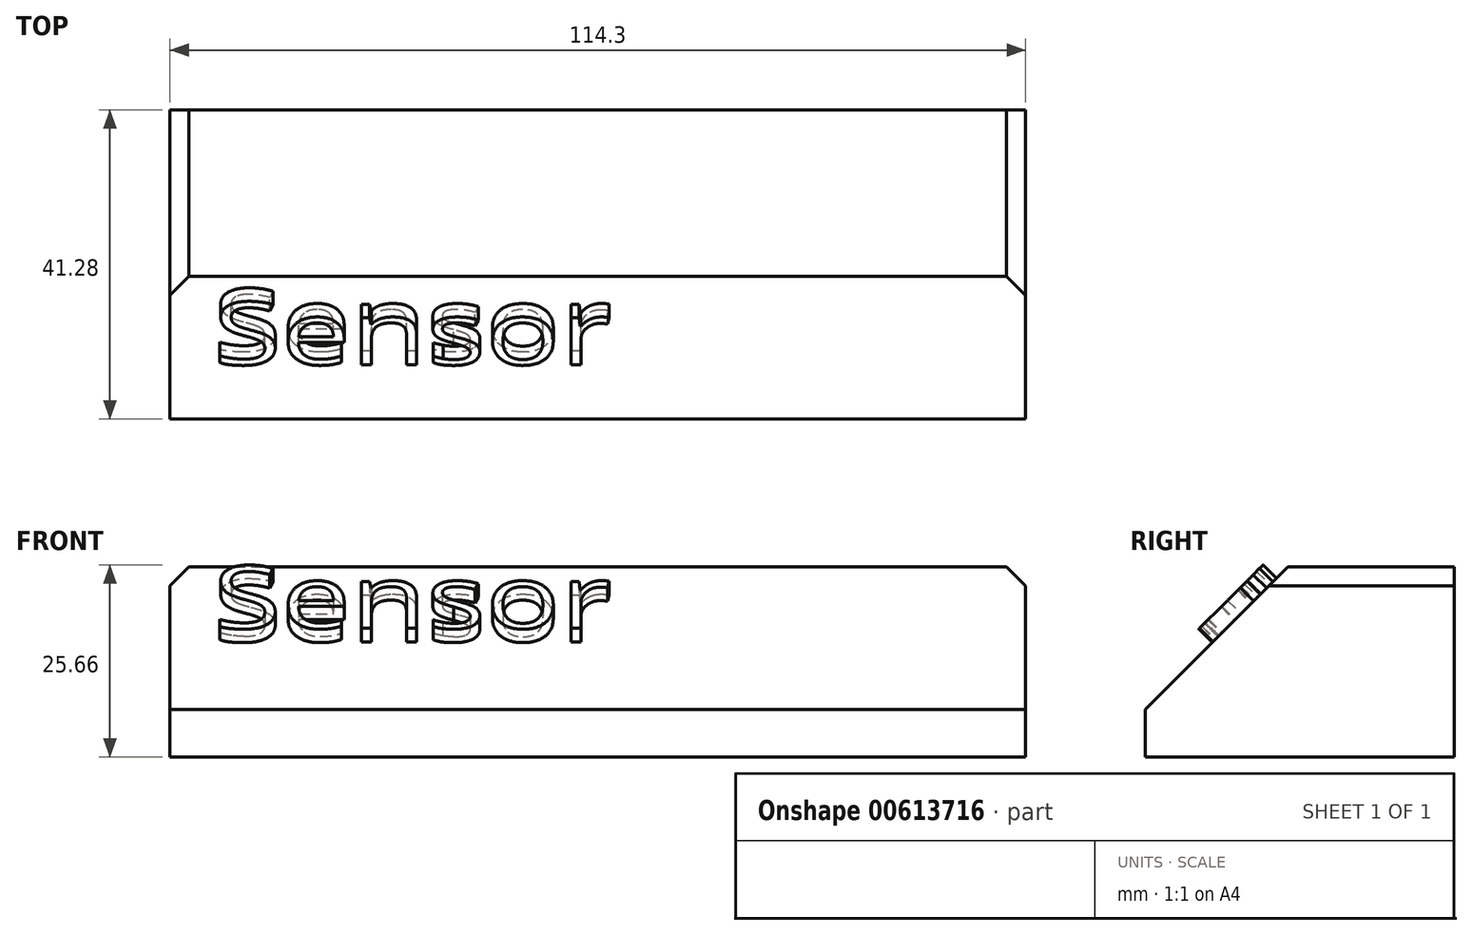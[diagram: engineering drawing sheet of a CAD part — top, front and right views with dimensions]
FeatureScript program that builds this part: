
annotation { "Feature Type Name" : "Feature", "Feature Type Description" : "" }
export const myFeature = defineFeature(function(context is Context, id is Id, definition is map)
    precondition{}
    {
        {
            var Q0;
            Q0=qCreatedBy(makeId("Top.planeOp"),FACE);
            var sketch = newSketch(context, id + "F0", { "sketchPlane" : qUnion([Q0])});
            skLineSegment(sketch, "E0.bottom", {"start": v(-57.15, 0) * mm, "end": v(57.15, 0) * mm});
            skLineSegment(sketch, "E0.top", {"start": v(-57.15, -41.28) * mm, "end": v(57.15, -41.28) * mm});
            skLineSegment(sketch, "E0.left", {"start": v(-57.15, 0) * mm, "end": v(-57.15, -41.28) * mm});
            skLineSegment(sketch, "E0.right", {"start": v(57.15, 0) * mm, "end": v(57.15, -41.28) * mm});
            skSolve(sketch);
        }
        {
            var Q0;
            Q0 = qSketchRegion(id + "F0", true);
            extrude(context, id + "F1", {"entities" : qUnion([Q0]), "depth" : 25.4 * mm, "offsetDistance" : 25.4 * mm});
        }
        {
            var Q0;
            Q0=makeQuery(id+"F1.opExtrude","CAP_EDGE",EDGE,{"disambiguationData":[OSD([sQuery(id+"F0.wireOp",EDGE,"E0.top")])],"isStart":false});
            chamfer(context, id + "F2", {"entities" : qUnion([Q0]), "width" : 19.05 * mm, "tangentPropagation" : true});
        }
        {
            var Q0;
            Q0=makeQuery(id+"F1.opExtrude","CAP_EDGE",EDGE,{"disambiguationData":[OSD([sQuery(id+"F0.wireOp",EDGE,"E0.right")])],"isStart":false});
            var Q1;
            Q1=makeQuery(id+"F1.opExtrude","CAP_EDGE",EDGE,{"disambiguationData":[OSD([sQuery(id+"F0.wireOp",EDGE,"E0.left")])],"isStart":false});
            chamfer(context, id + "F3", {"entities" : qUnion([Q0, Q1]), "width" : 2.54 * mm, "tangentPropagation" : true});
        }
        {
            var Q0;
            Q0=makeQuery(id+"F2.opChamfer","BLEND_FACE",FACE,{"disambiguationData":[OSD([sQuery(id+"F0.wireOp",EDGE,"E0.top")])]});
            var sketch = newSketch(context, id + "F4", { "sketchPlane" : qUnion([Q0])});
            skText(sketch, "E1", { "text": "Sensor", "fontName": "OpenSans-Regular.ttf"});
            const initialGuessF4  = {"E1": [-0.05137, -0.0119, 1, 0, 0.0119]};
            skSetInitialGuess(sketch, initialGuessF4);
            skSolve(sketch);
        }
        {
            var Q0;
            Q0 = qSketchRegion(id + "F4", true);
            extrude(context, id + "F5", {"entities" : qUnion([Q0]), "operationType" : NewBodyOperationType.ADD, "depth" : 2.54 * mm, "offsetDistance" : 25.4 * mm});
        }
    });
